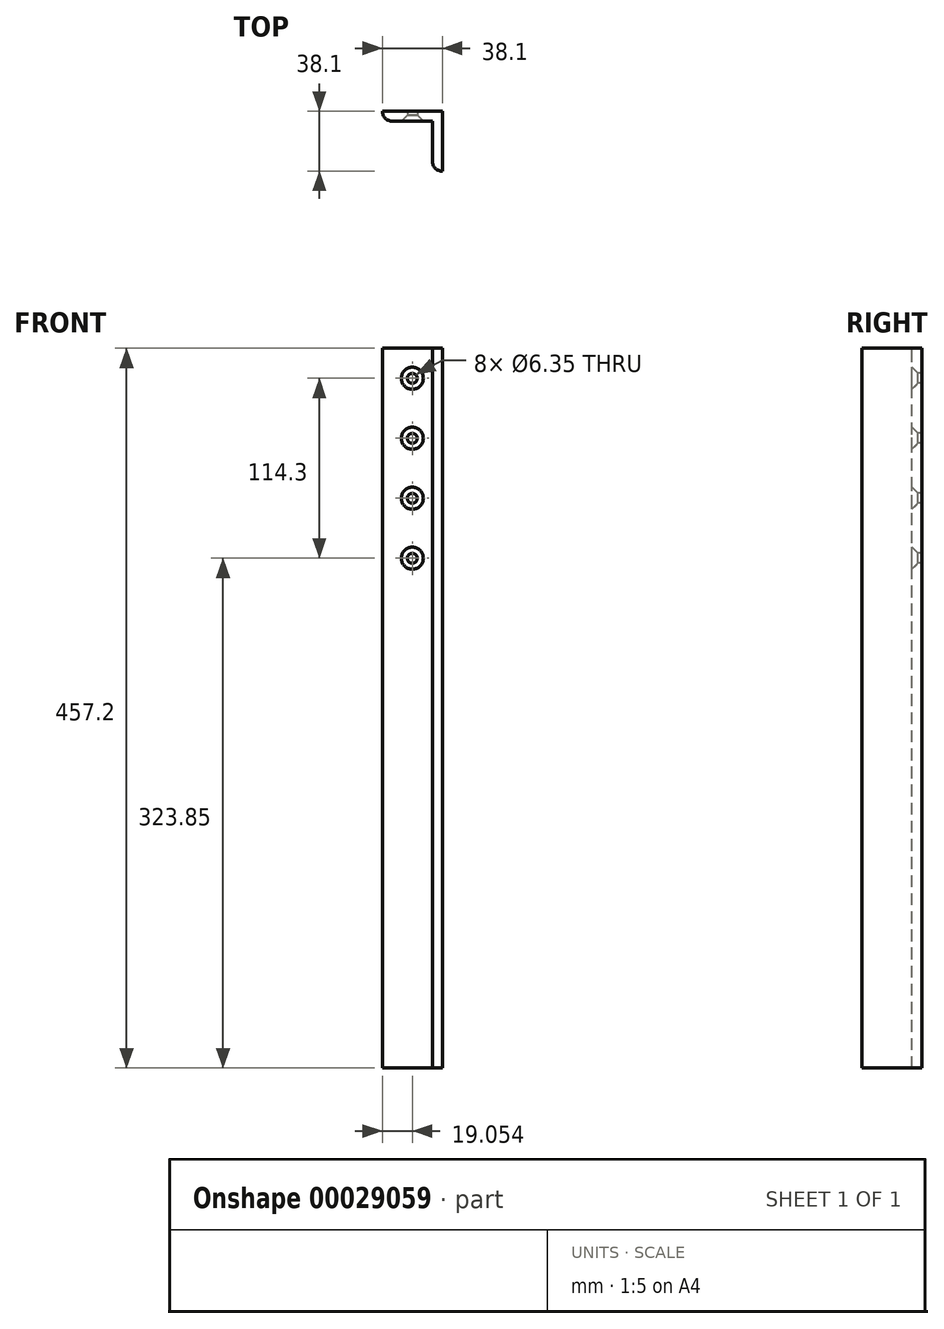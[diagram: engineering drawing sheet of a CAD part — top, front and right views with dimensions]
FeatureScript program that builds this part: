
annotation { "Feature Type Name" : "Feature", "Feature Type Description" : "" }
export const myFeature = defineFeature(function(context is Context, id is Id, definition is map)
    precondition{}
    {
        {
            var Q0;
            Q0=qCreatedBy(makeId("Top.planeOp"),FACE);
            var sketch = newSketch(context, id + "F0", { "sketchPlane" : qUnion([Q0])});
            skLineSegment(sketch, "E0.bottom", {"start": v(-21.42, 16.68) * mm, "end": v(16.68, 16.68) * mm});
            skLineSegment(sketch, "E0.top", {"start": v(-15.07, 10.33) * mm, "end": v(10.33, 10.33) * mm});
            skLineSegment(sketch, "E0.left", {"start": v(-21.42, 16.68) * mm, "end": v(-21.42, 16.68) * mm});
            skLineSegment(sketch, "E1.top", {"start": v(16.68, -21.42) * mm, "end": v(16.68, -21.42) * mm});
            skLineSegment(sketch, "E1.left", {"start": v(16.68, 16.68) * mm, "end": v(16.68, -21.42) * mm});
            skLineSegment(sketch, "E1.right", {"start": v(10.33, 10.33) * mm, "end": v(10.33, -15.07) * mm});
            skPoint(sketch, "E2.visualSharp", {"position": v(-21.42, 10.33) * mm});
            skArc(sketch, "E2.filletArc", {"start": v(-21.42, 16.68) * mm, "mid": v(-19.56, 12.2) * mm, "end": v(-15.07, 10.33) * mm});
            skPoint(sketch, "E3.visualSharp", {"position": v(10.33, -21.42) * mm});
            skArc(sketch, "E3.filletArc", {"start": v(10.33, -15.07) * mm, "mid": v(12.2, -19.56) * mm, "end": v(16.68, -21.42) * mm});
            skSolve(sketch);
        }
        {
            var Q0;
            Q0 = qSketchRegion(id + "F0", true);
            extrude(context, id + "F1", {"entities" : qUnion([Q0]), "oppositeDirection" : true, "depth" : 457.2 * mm});
        }
        {
            var Q0;
            Q0=makeQuery(id+"F1.opExtrude","SWEPT_FACE",FACE,{"disambiguationData":[OSD([sQuery(id+"F0.wireOp",EDGE,"E0.top")])]});
            var sketch = newSketch(context, id + "F2", { "sketchPlane" : qUnion([Q0])});
            skPoint(sketch, "E4", {"position": v(-2.37, -19.05) * mm});
            skPoint(sketch, "E5", {"position": v(-2.37, -57.15) * mm});
            skPoint(sketch, "E6", {"position": v(-2.37, -95.25) * mm});
            skPoint(sketch, "E7", {"position": v(-2.37, -133.35) * mm});
            skSolve(sketch);
        }
        {
            var Q0;
            Q0=sQuery(id+"F2.wireOp",VERTEX,"E4");
            var Q1;
            Q1=sQuery(id+"F2.wireOp",VERTEX,"E5");
            var Q2;
            Q2=sQuery(id+"F2.wireOp",VERTEX,"E6");
            var Q3;
            Q3=sQuery(id+"F2.wireOp",VERTEX,"E7");
            var Q4;
            Q4=makeQuery(id+"F1.opExtrude","SWEPT_BODY",BODY,{"disambiguationData":[OSD([sQuery(id+"F0.wireOp",EDGE,"E0.bottom"),sQuery(id+"F0.wireOp",EDGE,"E0.top"),sQuery(id+"F0.wireOp",EDGE,"E1.left"),sQuery(id+"F0.wireOp",EDGE,"E1.right"),sQuery(id+"F0.wireOp",EDGE,"E2.filletArc"),sQuery(id+"F0.wireOp",EDGE,"E3.filletArc")])]});
            hole(context, id + "F3", {"style" : HoleStyle.C_SINK, "holeDiameter" : 6.35 * mm, "cSinkDiameter" : 13.97 * mm, "endStyle" : HoleEndStyle.THROUGH, "locations" : qUnion([Q0, Q1, Q2, Q3]), "scope" : qUnion([Q4]), "cSinkAngle" : 90 * degree});
        }
    });
